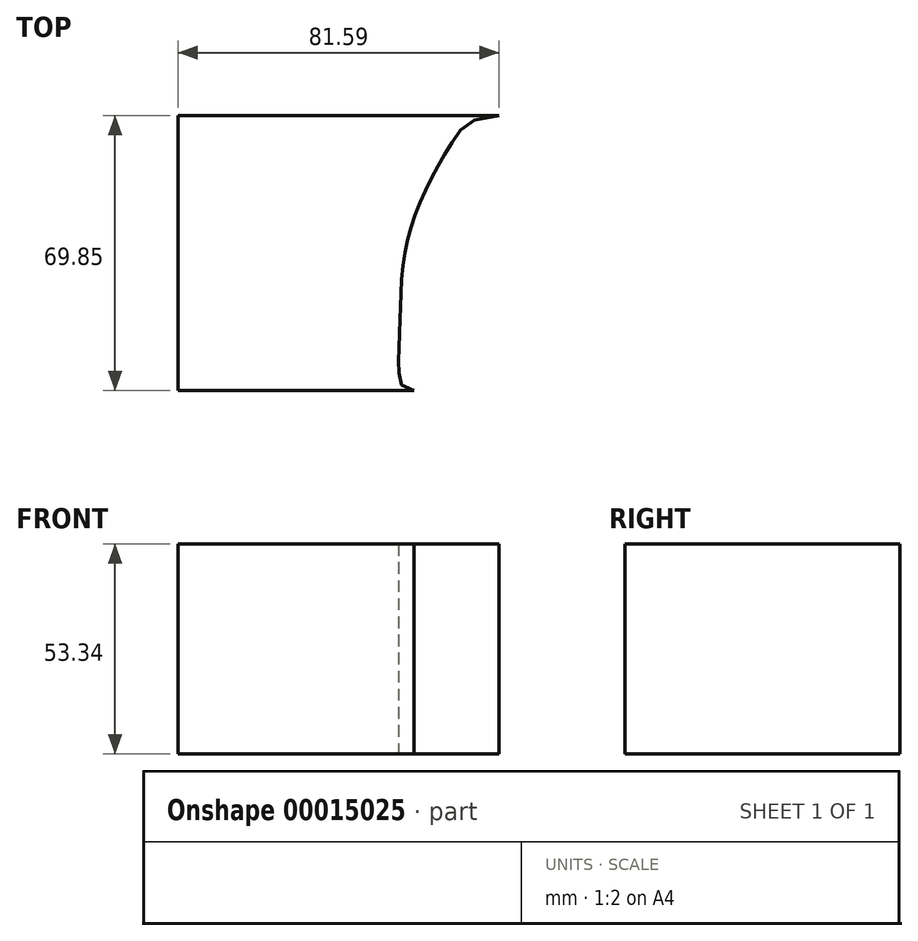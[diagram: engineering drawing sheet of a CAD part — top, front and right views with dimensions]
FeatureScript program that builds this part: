
annotation { "Feature Type Name" : "Feature", "Feature Type Description" : "" }
export const myFeature = defineFeature(function(context is Context, id is Id, definition is map)
    precondition{}
    {
        {
            var Q0;
            Q0=qCreatedBy(makeId("Top.planeOp"),FACE);
            var sketch = newSketch(context, id + "F0", { "sketchPlane" : qUnion([Q0])});
            skLineSegment(sketch, "E0", {"start": v(0, 0) * mm, "end": v(-21.59, 0) * mm});
            skFitSpline(sketch, "E1", {"points": [v(-21.59, 0) * mm, v(-25.4, 3.81) * mm, v(-25.46, 9.75) * mm, v(-25.2, 17.63) * mm, v(-24.97, 24.05) * mm, v(-24.47, 31.75) * mm, v(-23.33, 38.1) * mm, v(-21.4, 44.45) * mm, v(-18.76, 50.8) * mm, v(-15.47, 57.15) * mm, v(-11.68, 63.5) * mm, v(0, 69.85) * mm], "startDerivative": vector(-121.7, 0) * mm, "endDerivative": vector(185.92, 0) * mm});
            skLineSegment(sketch, "E2", {"start": v(0, 69.85) * mm, "end": v(-81.6, 69.85) * mm});
            skLineSegment(sketch, "E3", {"start": v(-81.6, 69.85) * mm, "end": v(-81.6, 0) * mm});
            skLineSegment(sketch, "E4", {"start": v(-81.6, 0) * mm, "end": v(-21.59, 0) * mm});
            skSolve(sketch);
        }
        {
            var Q0;
            Q0=makeQuery(id+"F0.imprint","IMPRINT",FACE,{"disambiguationData":[TD([[makeQuery(id+"F0.imprint","IMPRINT",EDGE,{"derivedFrom":sQuery(id+"F0.wireOp",EDGE,"E1")}),1.0]])]});
            extrude(context, id + "F1", {"entities" : qUnion([Q0]), "depth" : 53.34 * mm});
        }
    });
